# Revit family: _02HL_RU_Floor drain_HL510PrblueR
name_source: partatom
category: Instalační zařizovací předměty
units: mm (PartAtom-declared; Revit-internal decimal feet)

## family parameters
Bod výpočtu místnosti = Ano
Kóta kulaté spojky = Použít průměr
Nadpis OmniClass = Deck Waste Water Drains
Ořezat dutým tvarem při načtení = Ne
Sdílené = Ano
Typ dílu = Normální
Vždy vertikální = Ano
Založené na pracovní rovině = Ne
Číslo OmniClass = 23.70.50.21.24.14

## types (1)
- HL510PrblueR
    EAN = 9003076052189
    Indexovaná poznámka = HL510PrblueR
    Komentáře k typům = Трап для внутренних помещений DN40/50 горизонтальный с запахозапирающим устройством Primus blue, насадка круглая d 133мм/d 113мм.
    Model = HL510PrblueR
    Popis = Трап для внутренних помещений
    Přípoj CW = Ne
    Přípoj HW = Ne
    Přípoj odpadních dílů = Ano
    Přípoj ventilace = Ne
    URL = https://www.hutterer-lechner.com
    Výchozí výška = 0 mm  [stored 0 ft]
    Výrobce = HL Hutterer & Lechner GmbH
    ВЕС = 0,65 [kg]
    ВЫСОТА МОНТАЖА = 99 mm
    МАКСИМАЛЬНАЯ НАГРУЗКА КЛАССА = K3 - 300 kg
    МАТЕРИАЛ = PP, ABS
    НАСАДКА = 20-72 mm / d 133 mm
    НОМИНАЛЬНЫЙ ДИАМЕТР = 50 mm
    Нормы = EN 1253-8
    ПРОИЗВОДИТЕЛЬНОСТЬ = 0,5 l/s
    РАЗМЕР = DN40/50
    РЕШЁТКА = Rund d 113 mm

note: [stored X ft] marks values corroborated as IEEE doubles in the binary element streams (Revit-internal decimal feet)

## geometry (parser evidence)
native form markers: Sweep x33
no freeform markers — native parametric forms only
